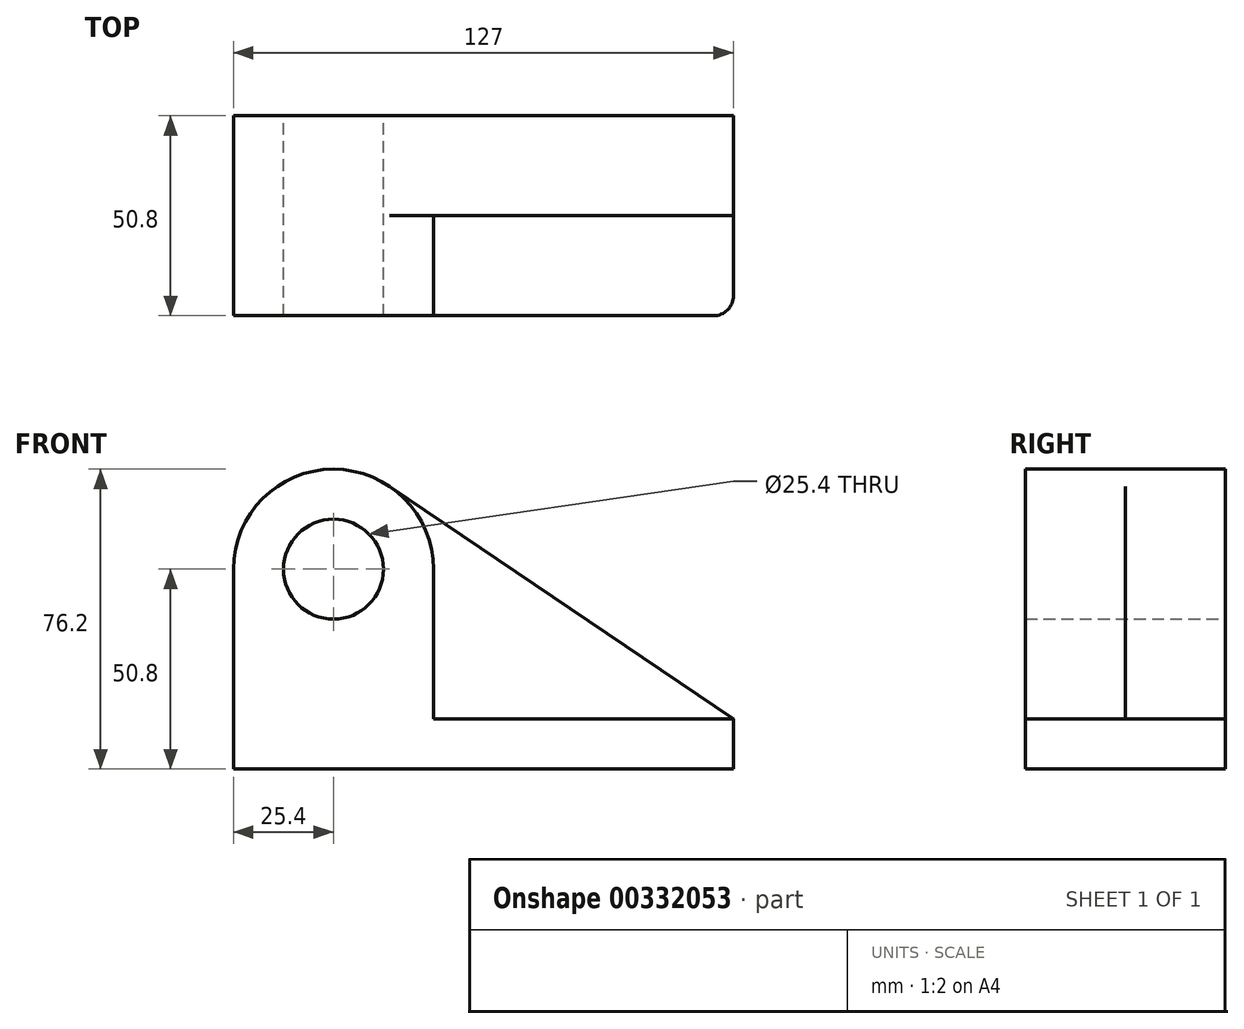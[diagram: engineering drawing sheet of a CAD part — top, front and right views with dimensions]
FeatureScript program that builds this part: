
annotation { "Feature Type Name" : "Feature", "Feature Type Description" : "" }
export const myFeature = defineFeature(function(context is Context, id is Id, definition is map)
    precondition{}
    {
        {
            var Q0;
            Q0=qCreatedBy(makeId("Front.planeOp"),FACE);
            var sketch = newSketch(context, id + "F0", { "sketchPlane" : qUnion([Q0])});
            skCircle(sketch, "E0", {"center": v(-36.86, 50.8) * mm, "radius": 12.7 * mm});
            skArc(sketch, "E1", {"start": v(-22.62, 71.83) * mm, "mid": v(-48.77, 73.24) * mm, "end": v(-62.26, 50.8) * mm});
            skLineSegment(sketch, "E2", {"start": v(-62.26, 50.8) * mm, "end": v(-62.26, 0) * mm});
            skLineSegment(sketch, "E3", {"start": v(-62.26, 0) * mm, "end": v(64.74, 0) * mm});
            skLineSegment(sketch, "E4", {"start": v(64.74, 0) * mm, "end": v(64.74, 12.7) * mm});
            skLineSegment(sketch, "E5", {"start": v(64.74, 12.7) * mm, "end": v(-22.62, 71.83) * mm});
            skSolve(sketch);
        }
        {
            var Q0;
            Q0=makeQuery(id+"F0.imprint","IMPRINT",FACE,{"disambiguationData":[TD([[makeQuery(id+"F0.imprint","IMPRINT",EDGE,{"derivedFrom":sQuery(id+"F0.wireOp",EDGE,"E0")}),-1.0]])]});
            extrude(context, id + "F1", {"entities" : qUnion([Q0]), "depth" : 25.4 * mm});
        }
        {
            var Q0;
            Q0=makeQuery(id+"F1.opExtrude","CAP_FACE",FACE,{"disambiguationData":[OSD([sQuery(id+"F0.wireOp",EDGE,"E0"),sQuery(id+"F0.wireOp",EDGE,"E1"),sQuery(id+"F0.wireOp",EDGE,"E2"),sQuery(id+"F0.wireOp",EDGE,"E3"),sQuery(id+"F0.wireOp",EDGE,"E4"),sQuery(id+"F0.wireOp",EDGE,"E5")])],"isStart":false});
            var sketch = newSketch(context, id + "F2", { "sketchPlane" : qUnion([Q0])});
            skCircle(sketch, "E6", {"center": v(-36.86, 50.8) * mm, "radius": 12.7 * mm});
            skLineSegment(sketch, "E7.bottom", {"start": v(64.74, 12.7) * mm, "end": v(-11.46, 12.7) * mm});
            skLineSegment(sketch, "E7.top", {"start": v(64.74, 0) * mm, "end": v(-62.26, 0) * mm});
            skLineSegment(sketch, "E7.left", {"start": v(64.74, 12.7) * mm, "end": v(64.74, 0) * mm});
            skLineSegment(sketch, "E7.right", {"start": v(-62.26, 12.7) * mm, "end": v(-62.26, 0) * mm});
            skArc(sketch, "E8", {"start": v(-11.46, 50.8) * mm, "mid": v(-36.86, 76.2) * mm, "end": v(-62.26, 50.8) * mm});
            skLineSegment(sketch, "E9", {"start": v(-62.26, 50.8) * mm, "end": v(-62.26, 12.7) * mm});
            skLineSegment(sketch, "E10", {"start": v(-11.46, 50.8) * mm, "end": v(-11.46, 12.7) * mm});
            skSolve(sketch);
        }
        {
            var Q0;
            Q0 = qSketchRegion(id + "F2", true);
            extrude(context, id + "F3", {"entities" : qUnion([Q0]), "operationType" : NewBodyOperationType.ADD, "depth" : 25.4 * mm});
        }
        {
            var Q0;
            Q0=makeQuery(id+"F2.imprint","IMPRINT",FACE,{"disambiguationData":[TD([[makeQuery(id+"F2.imprint","IMPRINT",EDGE,{"derivedFrom":sQuery(id+"F2.wireOp",EDGE,"E6")}),-1.0]])]});
            extrude(context, id + "F4", {"entities" : qUnion([Q0]), "operationType" : NewBodyOperationType.ADD, "depth" : 25.4 * mm});
        }
        {
            var Q0;
            Q0=makeQuery(id+"F3.opExtrude","CAP_EDGE",EDGE,{"disambiguationData":[OSD([sQuery(id+"F2.wireOp",EDGE,"E7.left")])],"isStart":false});
            fillet(context, id + "F5", {"entities" : qUnion([Q0]), "radius" : 5.08 * mm, "tangentPropagation" : true, "allowEdgeOverflow" : false});
        }
    });
